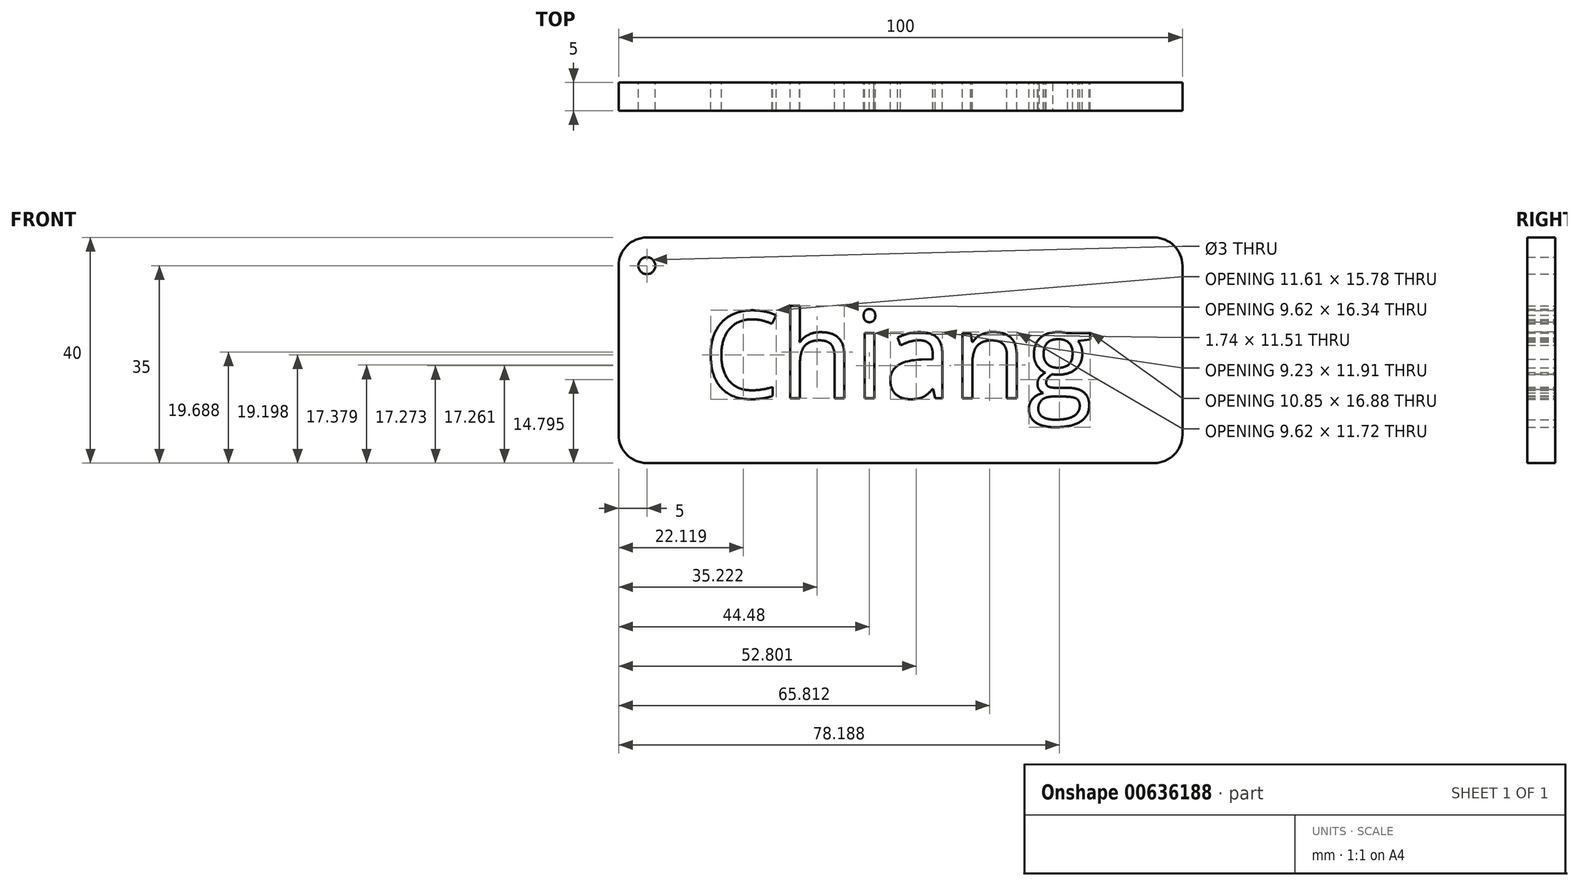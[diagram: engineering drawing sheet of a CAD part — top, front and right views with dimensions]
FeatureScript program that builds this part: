
annotation { "Feature Type Name" : "Feature", "Feature Type Description" : "" }
export const myFeature = defineFeature(function(context is Context, id is Id, definition is map)
    precondition{}
    {
        {
            var Q0;
            Q0=qCreatedBy(makeId("Front.planeOp"),FACE);
            var sketch = newSketch(context, id + "F0", { "sketchPlane" : qUnion([Q0])});
            skLineSegment(sketch, "E0.bottom", {"start": v(5, 0) * mm, "end": v(95, 0) * mm});
            skLineSegment(sketch, "E0.top", {"start": v(5, 40) * mm, "end": v(95, 40) * mm});
            skLineSegment(sketch, "E0.left", {"start": v(0, 5) * mm, "end": v(0, 35) * mm});
            skLineSegment(sketch, "E0.right", {"start": v(100, 5) * mm, "end": v(100, 35) * mm});
            skPoint(sketch, "E1.visualSharp", {"position": v(0, 40) * mm});
            skArc(sketch, "E1.filletArc", {"start": v(5, 40) * mm, "mid": v(1.46, 38.54) * mm, "end": v(0, 35) * mm});
            skPoint(sketch, "E2.visualSharp", {"position": v(0, 0) * mm});
            skArc(sketch, "E2.filletArc", {"start": v(0, 5) * mm, "mid": v(1.46, 1.46) * mm, "end": v(5, 0) * mm});
            skPoint(sketch, "E3.visualSharp", {"position": v(100, 0) * mm});
            skArc(sketch, "E3.filletArc", {"start": v(95, 0) * mm, "mid": v(98.54, 1.46) * mm, "end": v(100, 5) * mm});
            skPoint(sketch, "E4.visualSharp", {"position": v(100, 40) * mm});
            skArc(sketch, "E4.filletArc", {"start": v(100, 35) * mm, "mid": v(98.54, 38.54) * mm, "end": v(95, 40) * mm});
            skCircle(sketch, "E5", {"center": v(5, 35) * mm, "radius": 1.5 * mm});
            skLineSegment(sketch, "E6", {"start": v(5, 35) * mm, "end": v(5, 40) * mm, "construction": true});
            skLineSegment(sketch, "E7", {"start": v(5, 35) * mm, "end": v(0, 35) * mm, "construction": true});
            skText(sketch, "E8", { "text": "Chiang", "fontName": "OpenSans-Regular.ttf"});
            skLineSegment(sketch, "E9", {"start": v(15, 27) * mm, "end": v(15, 40) * mm, "construction": true});
            skLineSegment(sketch, "E10", {"start": v(15, 27) * mm, "end": v(0, 27) * mm, "construction": true});
            const initialGuessF0  = {"E8": [0.015, 0.01152, 1, 0, 0.01548]};
            skSetInitialGuess(sketch, initialGuessF0);
            skSolve(sketch);
        }
        {
            var Q0;
            Q0 = qSketchRegion(id + "F0", true);
            var Q1;
            Q1=makeQuery(id+"F0.imprint","IMPRINT",FACE,{"disambiguationData":[TD([[makeQuery(id+"F0.imprint","IMPRINT",EDGE,{"derivedFrom":sQuery(id+"F0.wireOp",EDGE,"E8.sketch_text.stroke-127")}),1.0]])]});
            var Q2;
            Q2=makeQuery(id+"F0.imprint","IMPRINT",FACE,{"disambiguationData":[TD([[makeQuery(id+"F0.imprint","IMPRINT",EDGE,{"derivedFrom":sQuery(id+"F0.wireOp",EDGE,"E8.sketch_text.stroke-118")}),1.0]])]});
            extrude(context, id + "F1", {"entities" : qUnion([Q0, Q1, Q2]), "depth" : 5 * mm, "offsetDistance" : 25 * mm});
        }
    });
